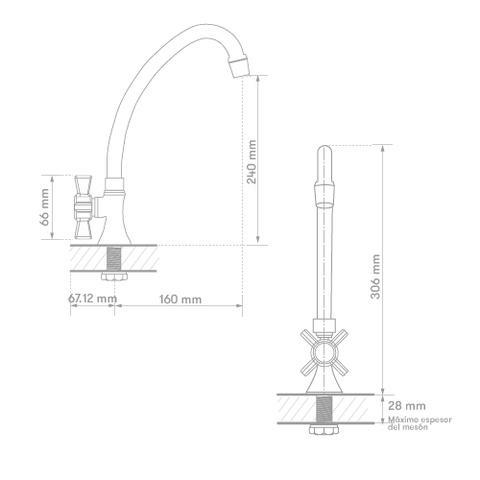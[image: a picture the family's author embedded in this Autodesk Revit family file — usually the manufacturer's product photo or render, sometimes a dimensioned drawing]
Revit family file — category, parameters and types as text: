
# Revit family: II-BR07-11-BRAZO ARCO MÓVIL LAVAPLATOS
name_source: partatom
category: Plumbing Fixtures
revit_build: Autodesk Revit 2018 (Build: 20170223_1515(x64)
units: mm (PartAtom-declared; Revit-internal decimal feet)

## family parameters
Cut with Voids When Loaded = No
Host = Face
OmniClass Number = 23.31.11.00
Part Type = Normal
Room Calculation Point = No
Round Connector Dimension = Use Diameter
Shared = No

## types (1)
- II-BR07-11
    Alto = 294 mm  [stored 0.964567 ft]
    Ancho = 54 mm  [stored 0.177165 ft]
    CW Connection = Yes
    Default Elevation = 0 mm  [stored 0 ft]
    Description = Brazo Griferia Cocina
    HW Connection = Yes
    Link Ficha Tecnica = https://infotecnica.gricol.com
    Manufacturer = Gricol
    Model = II-BR07-11
    Plastico ABS Cromado = Metal Laton Cromado
    Product Name = BRAZO ARCO MÓVIL LAVAPLATOS
    Profundidad = 185 mm  [stored 0.606955 ft]
    Type Image = FOTO BRAZO ARCO MÓVIL LAVAPLATOS.jpg
    URL = https://www.gricol.com
    Vent Connection = No
    Waste Connection = No

note: [stored X ft] marks values corroborated as IEEE doubles in the binary element streams (Revit-internal decimal feet)

## geometry (parser evidence)
native form markers: Blend x2, Sweep x5
no freeform markers — native parametric forms only
